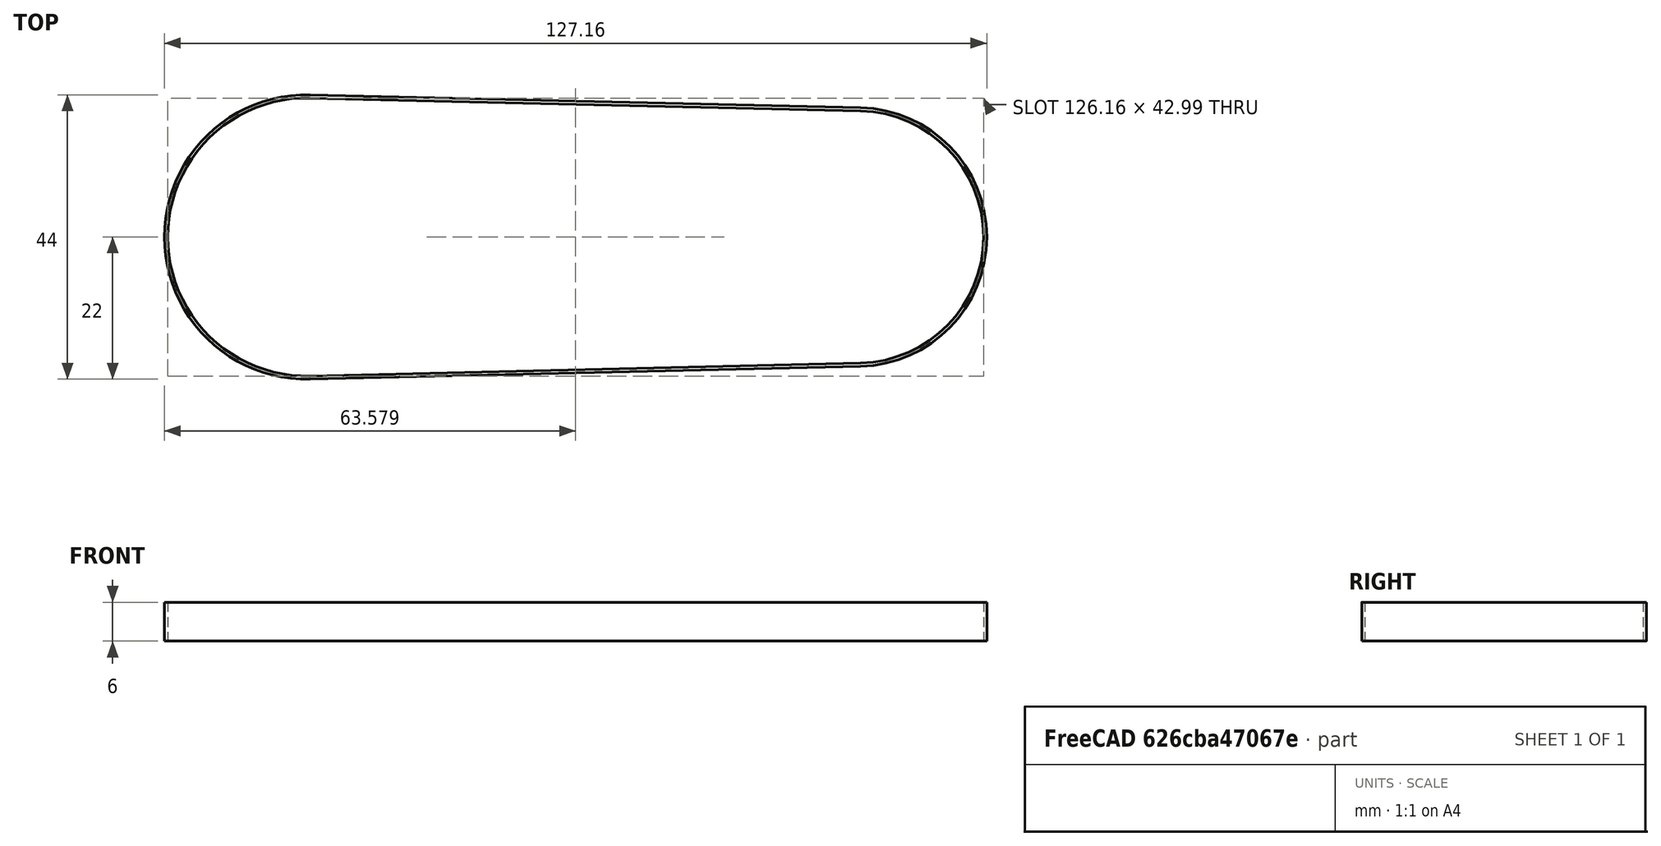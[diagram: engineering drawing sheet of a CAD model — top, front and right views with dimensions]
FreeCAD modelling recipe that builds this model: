
FCSTD DOCUMENT  (FreeCAD 0.20R29177 +426 (Git))
Label: belt
License: All rights reserved
LicenseURL: http://en.wikipedia.org/wiki/All_rights_reserved
objects: PartDesign::CoordinateSystem×2, Sketcher::SketchObject×1, PartDesign::Pad×1, PartDesign::Body×1
note: 6 computed .brp shape members not serialized (recipe doc carries the construction recipe); baked Part::Feature solids carry a one-line shape summary decoded from their .brp

FEATURE [Sketcher::SketchObject] Sketch
  FullyConstrained = false
  MapMode = 5
  Support = -> [XY_Plane]
  sketch-geometry (8):
    g0: ArcOfCircle CenterX=-31.4005 CenterY=0 CenterZ=0 NormalX=0 NormalY=0 NormalZ=1 AngleXU=0 Radius=21.5 StartAngle=1.54731 EndAngle=4.73588
    g1: ArcOfCircle CenterX=53.7587 CenterY=0 CenterZ=0 NormalX=0 NormalY=0 NormalZ=1 AngleXU=0 Radius=19.5 StartAngle=4.73588 EndAngle=7.83049
    g2: LineSegment StartX=-30.8955 StartY=21.4941 StartZ=0 EndX=54.2167 EndY=19.4946 EndZ=0
    g3: LineSegment StartX=-30.8955 StartY=-21.4941 StartZ=0 EndX=54.2167 EndY=-19.4946 EndZ=0
    g4: ArcOfCircle CenterX=-31.4005 CenterY=0 CenterZ=0 NormalX=0 NormalY=0 NormalZ=1 AngleXU=0 Radius=22 StartAngle=1.54731 EndAngle=4.73588
    g5: ArcOfCircle CenterX=53.7587 CenterY=0 CenterZ=0 NormalX=0 NormalY=0 NormalZ=1 AngleXU=0 Radius=20 StartAngle=4.73588 EndAngle=7.83049
    g6: LineSegment StartX=-30.8838 StartY=21.9939 StartZ=0 EndX=54.2284 EndY=19.9945 EndZ=0
    g7: LineSegment StartX=-30.8838 StartY=-21.9939 StartZ=0 EndX=54.2284 EndY=-19.9945 EndZ=0
  constraints (16):
    c: PointOnObject(g0,g-1)
    c: Diameter(g0) = 43
    c: PointOnObject(g1,g-1)
    c: Diameter(g1) = 39
    c: Tangent(g0,g3) = -1.5708
    c: Tangent(g0,g2) = 1.5708
    c: Tangent(g1,g2) = 1.5708
    c: Tangent(g1,g3) = -1.5708
    c: Diameter(g4) = 44
    c: Diameter(g5) = 40
    c: Tangent(g4,g7) = -1.5708
    c: Tangent(g4,g6) = 1.5708
    c: Tangent(g5,g6) = 1.5708
    c: Tangent(g5,g7) = -1.5708
    c: Coincident(g4,g0)
    c: Coincident(g5,g1)
FEATURE [PartDesign::Pad] Pad
  Direction = (0,0,1)
  Length = 6
  Length2 = 10
  Profile = -> Sketch
  ReferenceAxis = -> Sketch [N_Axis]
  Type = 0
FEATURE [PartDesign::CoordinateSystem] LCS_gear60
  AttacherType = Attacher::AttachEngine3D
  MapMode = 12
  Placement = pos=(53.7587,-3.3e-15,6) rot=(0.58639,-0.572777,-0.572777;2.08089rad)
  Support = -> [Pad]
FEATURE [PartDesign::CoordinateSystem] LCS_gear66
  AttacherType = Attacher::AttachEngine3D
  AttachmentOffset = pos=(0,-5,0) rot=(0,0,1;0rad)
  MapMode = 12
  Placement = pos=(-31.4005,4.1e-15,1) rot=(0.58639,0.572777,0.572777;2.08089rad)
  Support = -> [Pad]
FEATURE [PartDesign::Body] Body  label="belt_Body"
  Group = -> [Sketch,Pad,LCS_gear60,LCS_gear66]
  Origin = -> Origin
  Tip = -> Pad
